# Revit family: Plumbing Fixture_Galvin_CliniLever_Wall_Mixer_CP-BS_TC51FC1C_W
name_source: partatom
category: Plumbing Fixtures
units: mm (PartAtom-declared; Revit-internal decimal feet)

## family parameters
Cut with Voids When Loaded = No
Host = Face
Part Type = Normal
Room Calculation Point = No
Round Connector Dimension = Use Diameter
Shared = No

## types (1)
- Type 1
    Anti_Ligature = No
    Application = Commercial
    CW Connection = Yes
    CategoryStyleOrType_ANZRS = Plumbing Fixture
    Default Elevation = 0 mm  [stored 0 ft]
    Description = CLINILEVER CHROME PLATED BRASS HOSPITAL WALL MIXING SET TYPE 51 FIXED 150 C/D
    FlowRate = 6.74
    HW Connection = Yes
    Instructions = https://www.galvinengineering.com.au
    Manufacturer = Galvin Engineering
    Manufacturer_OverallDepth = 0 mm  [stored 0 ft]
    Manufacturer_OverallHeight = 0 mm  [stored 0 ft]
    Manufacturer_OverallWidth = 0 mm  [stored 0 ft]
    Mounting = Wall
    Mounting_Surface = Wall
    PlumbingFinish = Chrome
    PlumbingMaterial_ANZRS = Brass
    Product_Range = CliniLever
    Product_Type = Mixer
    SKU_Code = TC51FC1C
    Specify_Host = Face
    Thread = 1/2" BSP F
    URL = http://www.galvinengineering.com.au
    Vandal_Resistant = No
    Variants = Ceramic
    Vent Connection = No
    Waste Connection = No

note: [stored X ft] marks values corroborated as IEEE doubles in the binary element streams (Revit-internal decimal feet)

## geometry (parser evidence)
native form markers: Sweep x5
no freeform markers — native parametric forms only
